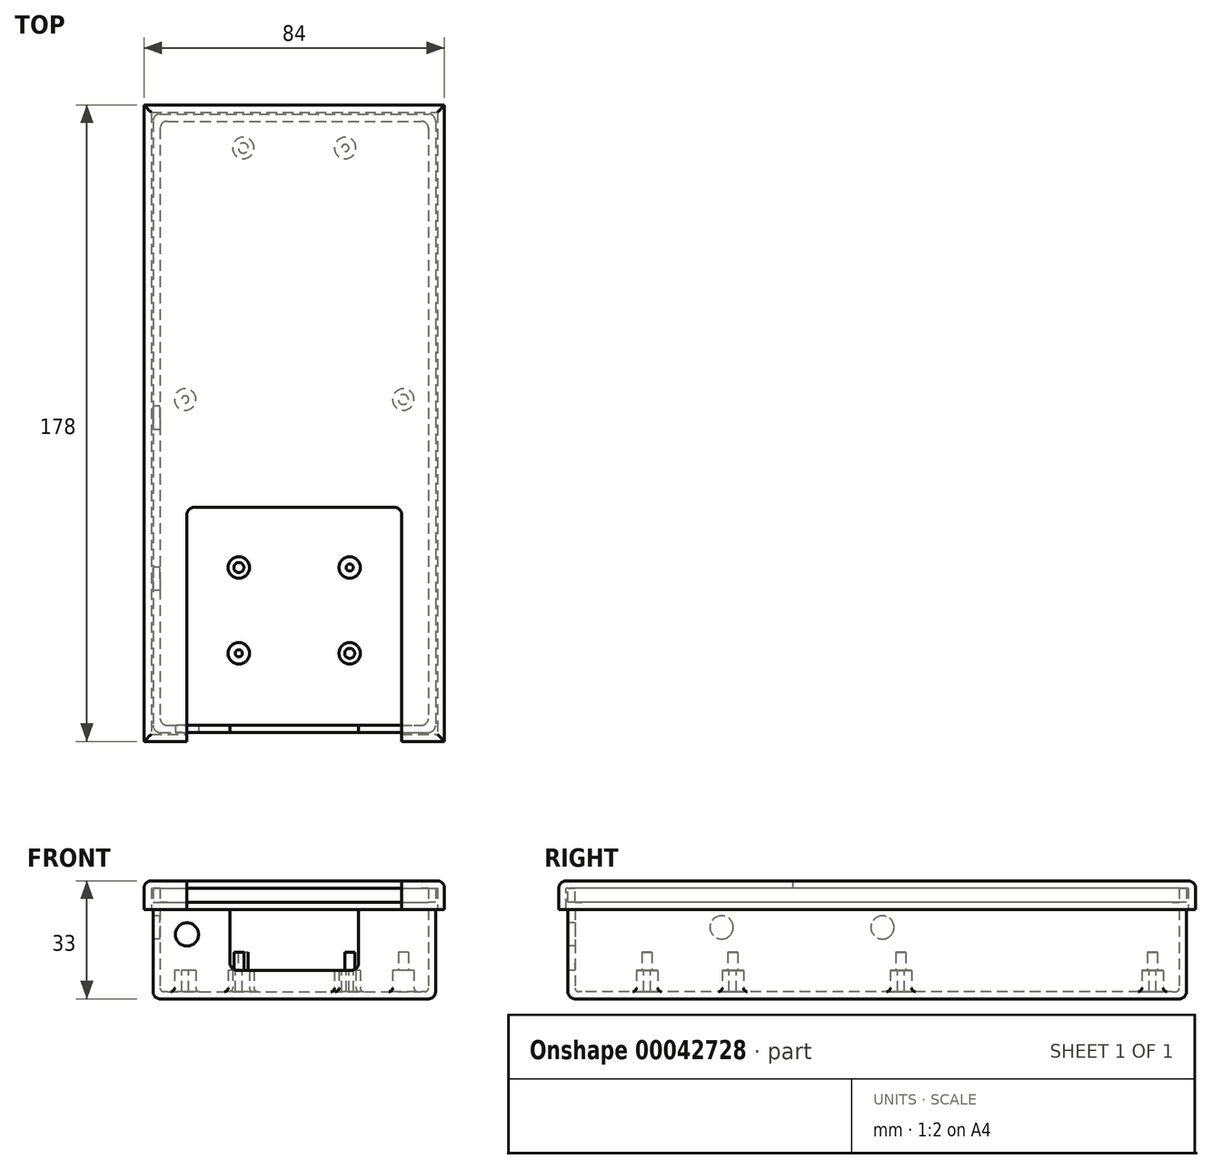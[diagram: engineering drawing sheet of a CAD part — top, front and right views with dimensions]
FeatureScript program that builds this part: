
annotation { "Feature Type Name" : "Feature", "Feature Type Description" : "" }
export const myFeature = defineFeature(function(context is Context, id is Id, definition is map)
    precondition{}
    {
        {
            var Q0;
            Q0=qCreatedBy(makeId("Top.planeOp"),FACE);
            var sketch = newSketch(context, id + "F0", { "sketchPlane" : qUnion([Q0])});
            skLineSegment(sketch, "E0.bottom", {"start": v(-37.5, 83) * mm, "end": v(37.5, 83) * mm});
            skLineSegment(sketch, "E0.top", {"start": v(-37.5, -86) * mm, "end": v(37.5, -86) * mm});
            skLineSegment(sketch, "E0.left", {"start": v(-37.5, 83) * mm, "end": v(-37.5, -86) * mm});
            skLineSegment(sketch, "E0.right", {"start": v(37.5, 83) * mm, "end": v(37.5, -86) * mm});
            skCircle(sketch, "E1", {"center": v(-14.25, 75.5) * mm, "radius": 3 * mm});
            skCircle(sketch, "E2", {"center": v(14.25, 75.5) * mm, "radius": 3 * mm});
            skCircle(sketch, "E3", {"center": v(30.5, 5.15) * mm, "radius": 3 * mm});
            skCircle(sketch, "E4", {"center": v(-30.5, 5.15) * mm, "radius": 3 * mm});
            skLineSegment(sketch, "E5.0", {"start": v(-39.5, 85) * mm, "end": v(39.5, 85) * mm});
            skLineSegment(sketch, "E5.1", {"start": v(-39.5, 85) * mm, "end": v(-39.5, -88) * mm});
            skLineSegment(sketch, "E5.2", {"start": v(-39.5, -88) * mm, "end": v(39.5, -88) * mm});
            skLineSegment(sketch, "E5.3", {"start": v(39.5, 85) * mm, "end": v(39.5, -88) * mm});
            skCircle(sketch, "E6", {"center": v(15.5, -41.85) * mm, "radius": 3 * mm});
            skCircle(sketch, "E7", {"center": v(-15.5, -41.85) * mm, "radius": 3 * mm});
            skCircle(sketch, "E8", {"center": v(15.5, -65.85) * mm, "radius": 3 * mm});
            skCircle(sketch, "E9", {"center": v(-15.5, -65.85) * mm, "radius": 3 * mm});
            skSolve(sketch);
        }
        {
            var Q0;
            Q0=makeQuery(id+"F0.imprint","IMPRINT",FACE,{"disambiguationData":[TD([[makeQuery(id+"F0.imprint","IMPRINT",EDGE,{"derivedFrom":sQuery(id+"F0.wireOp",EDGE,"E0.bottom")}),-1.0]])]});
            extrude(context, id + "F1", {"entities" : qUnion([Q0]), "depth" : 2 * mm});
        }
        {
            var Q0;
            Q0=makeQuery(id+"F0.imprint","IMPRINT",FACE,{"disambiguationData":[TD([[makeQuery(id+"F0.imprint","IMPRINT",EDGE,{"derivedFrom":sQuery(id+"F0.wireOp",EDGE,"E0.bottom")}),1.0]])]});
            extrude(context, id + "F2", {"entities" : qUnion([Q0]), "operationType" : NewBodyOperationType.ADD, "depth" : 25 * mm});
        }
        {
            var Q0;
            Q0=makeQuery(id+"F0.imprint","IMPRINT",FACE,{"disambiguationData":[TD([[makeQuery(id+"F0.imprint","IMPRINT",EDGE,{"derivedFrom":sQuery(id+"F0.wireOp",EDGE,"E1")}),1.0]])]});
            var Q1;
            Q1=makeQuery(id+"F0.imprint","IMPRINT",FACE,{"disambiguationData":[TD([[makeQuery(id+"F0.imprint","IMPRINT",EDGE,{"derivedFrom":sQuery(id+"F0.wireOp",EDGE,"E2")}),1.0]])]});
            var Q2;
            Q2=makeQuery(id+"F0.imprint","IMPRINT",FACE,{"disambiguationData":[TD([[makeQuery(id+"F0.imprint","IMPRINT",EDGE,{"derivedFrom":sQuery(id+"F0.wireOp",EDGE,"E3")}),1.0]])]});
            var Q3;
            Q3=makeQuery(id+"F0.imprint","IMPRINT",FACE,{"disambiguationData":[TD([[makeQuery(id+"F0.imprint","IMPRINT",EDGE,{"derivedFrom":sQuery(id+"F0.wireOp",EDGE,"E4")}),1.0]])]});
            var Q4;
            Q4=makeQuery(id+"F0.imprint","IMPRINT",FACE,{"disambiguationData":[TD([[makeQuery(id+"F0.imprint","IMPRINT",EDGE,{"derivedFrom":sQuery(id+"F0.wireOp",EDGE,"E6")}),1.0]])]});
            var Q5;
            Q5=makeQuery(id+"F0.imprint","IMPRINT",FACE,{"disambiguationData":[TD([[makeQuery(id+"F0.imprint","IMPRINT",EDGE,{"derivedFrom":sQuery(id+"F0.wireOp",EDGE,"E8")}),1.0]])]});
            var Q6;
            Q6=makeQuery(id+"F0.imprint","IMPRINT",FACE,{"disambiguationData":[TD([[makeQuery(id+"F0.imprint","IMPRINT",EDGE,{"derivedFrom":sQuery(id+"F0.wireOp",EDGE,"E7")}),1.0]])]});
            var Q7;
            Q7=makeQuery(id+"F0.imprint","IMPRINT",FACE,{"disambiguationData":[TD([[makeQuery(id+"F0.imprint","IMPRINT",EDGE,{"derivedFrom":sQuery(id+"F0.wireOp",EDGE,"E9")}),1.0]])]});
            extrude(context, id + "F3", {"entities" : qUnion([Q0, Q1, Q2, Q3, Q4, Q5, Q6, Q7]), "operationType" : NewBodyOperationType.ADD, "depth" : 8 * mm});
        }
        {
            var Q0;
            Q0=makeQuery(id+"F3.opExtrude","CAP_FACE",FACE,{"disambiguationData":[OSD([sQuery(id+"F0.wireOp",EDGE,"E1")])],"isStart":false});
            var sketch = newSketch(context, id + "F4", { "sketchPlane" : qUnion([Q0])});
            skCircle(sketch, "E10", {"center": v(-14.25, 75.5) * mm, "radius": 1.4 * mm});
            skCircle(sketch, "E11", {"center": v(30.5, 5.15) * mm, "radius": 1.4 * mm});
            skCircle(sketch, "E12", {"center": v(-15.5, -41.85) * mm, "radius": 1.4 * mm});
            skCircle(sketch, "E13", {"center": v(15.5, -65.85) * mm, "radius": 1.4 * mm});
            skCircle(sketch, "E14", {"center": v(14.25, 75.5) * mm, "radius": 1 * mm});
            skCircle(sketch, "E15", {"center": v(-30.5, 5.15) * mm, "radius": 1 * mm});
            skCircle(sketch, "E16", {"center": v(15.5, -41.85) * mm, "radius": 1 * mm});
            skCircle(sketch, "E17", {"center": v(-15.5, -65.85) * mm, "radius": 1 * mm});
            skSolve(sketch);
        }
        {
            var Q0;
            Q0=makeQuery(id+"F4.imprint","IMPRINT",FACE,{"disambiguationData":[TD([[makeQuery(id+"F4.imprint","IMPRINT",EDGE,{"derivedFrom":sQuery(id+"F4.wireOp",EDGE,"E10")}),1.0]])]});
            var Q1;
            Q1=makeQuery(id+"F4.imprint","IMPRINT",FACE,{"disambiguationData":[TD([[makeQuery(id+"F4.imprint","IMPRINT",EDGE,{"derivedFrom":sQuery(id+"F4.wireOp",EDGE,"E11")}),1.0]])]});
            var Q2;
            Q2=makeQuery(id+"F4.imprint","IMPRINT",FACE,{"disambiguationData":[TD([[makeQuery(id+"F4.imprint","IMPRINT",EDGE,{"derivedFrom":sQuery(id+"F4.wireOp",EDGE,"E12")}),1.0]])]});
            var Q3;
            Q3=makeQuery(id+"F4.imprint","IMPRINT",FACE,{"disambiguationData":[TD([[makeQuery(id+"F4.imprint","IMPRINT",EDGE,{"derivedFrom":sQuery(id+"F4.wireOp",EDGE,"E13")}),1.0]])]});
            var Q4;
            Q4=sQuery(id+"F4.wireOp",EDGE,"E13");
            var Q5;
            Q5=sQuery(id+"F4.wireOp",EDGE,"E12");
            var Q6;
            Q6=sQuery(id+"F4.wireOp",EDGE,"E11");
            var Q7;
            Q7=sQuery(id+"F4.wireOp",EDGE,"E10");
            extrude(context, id + "F5", {"entities" : qUnion([Q0, Q1, Q2, Q3]), "operationType" : NewBodyOperationType.ADD, "surfaceEntities" : qUnion([Q4, Q5, Q6, Q7]), "depth" : 5 * mm});
        }
        {
            var Q0;
            Q0=makeQuery(id+"F4.imprint","IMPRINT",FACE,{"disambiguationData":[TD([[makeQuery(id+"F4.imprint","IMPRINT",EDGE,{"derivedFrom":sQuery(id+"F4.wireOp",EDGE,"E14")}),1.0]])]});
            var Q1;
            Q1=makeQuery(id+"F4.imprint","IMPRINT",FACE,{"disambiguationData":[TD([[makeQuery(id+"F4.imprint","IMPRINT",EDGE,{"derivedFrom":sQuery(id+"F4.wireOp",EDGE,"E15")}),1.0]])]});
            var Q2;
            Q2=makeQuery(id+"F4.imprint","IMPRINT",FACE,{"disambiguationData":[TD([[makeQuery(id+"F4.imprint","IMPRINT",EDGE,{"derivedFrom":sQuery(id+"F4.wireOp",EDGE,"E16")}),1.0]])]});
            var Q3;
            Q3=makeQuery(id+"F4.imprint","IMPRINT",FACE,{"disambiguationData":[TD([[makeQuery(id+"F4.imprint","IMPRINT",EDGE,{"derivedFrom":sQuery(id+"F4.wireOp",EDGE,"E17")}),1.0]])]});
            extrude(context, id + "F6", {"entities" : qUnion([Q0, Q1, Q2, Q3]), "operationType" : NewBodyOperationType.REMOVE, "oppositeDirection" : true, "depth" : 6 * mm});
        }
        {
            var Q0;
            Q0=makeQuery(id+"F2.opExtrude","SWEPT_FACE",FACE,{"disambiguationData":[OSD([sQuery(id+"F0.wireOp",EDGE,"E5.2")])]});
            var sketch = newSketch(context, id + "F7", { "sketchPlane" : qUnion([Q0])});
            skLineSegment(sketch, "E18.bottom", {"start": v(-18, 25) * mm, "end": v(18, 25) * mm});
            skLineSegment(sketch, "E18.top", {"start": v(-18, 8) * mm, "end": v(18, 8) * mm});
            skLineSegment(sketch, "E18.left", {"start": v(-18, 25) * mm, "end": v(-18, 8) * mm});
            skLineSegment(sketch, "E18.right", {"start": v(18, 25) * mm, "end": v(18, 8) * mm});
            skSolve(sketch);
        }
        {
            var Q0;
            Q0=makeQuery(id+"F7.imprint","IMPRINT",FACE,{"disambiguationData":[TD([[makeQuery(id+"F7.imprint","IMPRINT",EDGE,{"derivedFrom":sQuery(id+"F7.wireOp",EDGE,"E18.bottom")}),-1.0]])]});
            extrude(context, id + "F8", {"entities" : qUnion([Q0]), "operationType" : NewBodyOperationType.REMOVE, "endBound" : BoundingType.UP_TO_NEXT, "oppositeDirection" : true, "depth" : 25 * mm});
        }
        {
            var Q0;
            {var subQ0=sQuery(id+"F0.wireOp",EDGE,"E0.bottom");var subQ1=sQuery(id+"F0.wireOp",EDGE,"E0.top");var subQ2=sQuery(id+"F0.wireOp",EDGE,"E0.left");var subQ3=sQuery(id+"F0.wireOp",EDGE,"E0.right");var subQ4=sQuery(id+"F0.wireOp",EDGE,"E1");var subQ5=sQuery(id+"F0.wireOp",EDGE,"E2");var subQ6=sQuery(id+"F0.wireOp",EDGE,"E3");var subQ7=sQuery(id+"F0.wireOp",EDGE,"E4");var subQ8=sQuery(id+"F0.wireOp",EDGE,"E6");var subQ9=sQuery(id+"F0.wireOp",EDGE,"E7");var subQ10=sQuery(id+"F0.wireOp",EDGE,"E8");var subQ11=sQuery(id+"F0.wireOp",EDGE,"E9");Q0=makeQuery(id+"F3.boolean.opBoolean","MERGE",FACE,{"derivedFrom":[makeQuery(id+"F2.boolean.opBoolean","MERGE",FACE,{"derivedFrom":[makeQuery(id+"F1.opExtrude","CAP_FACE",FACE,{"disambiguationData":[OSD([subQ0,subQ1,subQ2,subQ3,subQ4,subQ5,subQ6,subQ7,subQ8,subQ9,subQ10,subQ11])],"isStart":true}),makeQuery(id+"F2.opExtrude","CAP_FACE",FACE,{"disambiguationData":[OSD([subQ0,subQ1,subQ2,subQ3,sQuery(id+"F0.wireOp",EDGE,"E5.0"),sQuery(id+"F0.wireOp",EDGE,"E5.1"),sQuery(id+"F0.wireOp",EDGE,"E5.2"),sQuery(id+"F0.wireOp",EDGE,"E5.3")])],"isStart":true})]}),makeQuery(id+"F3.opExtrude","CAP_FACE",FACE,{"disambiguationData":[OSD([subQ4])],"isStart":true}),makeQuery(id+"F3.opExtrude","CAP_FACE",FACE,{"disambiguationData":[OSD([subQ5])],"isStart":true}),makeQuery(id+"F3.opExtrude","CAP_FACE",FACE,{"disambiguationData":[OSD([subQ6])],"isStart":true}),makeQuery(id+"F3.opExtrude","CAP_FACE",FACE,{"disambiguationData":[OSD([subQ7])],"isStart":true}),makeQuery(id+"F3.opExtrude","CAP_FACE",FACE,{"disambiguationData":[OSD([subQ8])],"isStart":true}),makeQuery(id+"F3.opExtrude","CAP_FACE",FACE,{"disambiguationData":[OSD([subQ9])],"isStart":true}),makeQuery(id+"F3.opExtrude","CAP_FACE",FACE,{"disambiguationData":[OSD([subQ10])],"isStart":true}),makeQuery(id+"F3.opExtrude","CAP_FACE",FACE,{"disambiguationData":[OSD([subQ11])],"isStart":true})]});}
            var sketch = newSketch(context, id + "F9", { "sketchPlane" : qUnion([Q0])});
            skCircle(sketch, "E19", {"center": v(-30, 75) * mm, "radius": 3 * mm});
            skCircle(sketch, "E20", {"center": v(30, 75) * mm, "radius": 3 * mm});
            skCircle(sketch, "E21", {"center": v(-30, -75) * mm, "radius": 3 * mm});
            skCircle(sketch, "E22", {"center": v(30, -75) * mm, "radius": 3 * mm});
            skLineSegment(sketch, "E23", {"start": v(-55.2, 75) * mm, "end": v(65.62, 75) * mm, "construction": true});
            skLineSegment(sketch, "E24", {"start": v(-55.2, -75) * mm, "end": v(62.26, -75) * mm, "construction": true});
            skSolve(sketch);
        }
        {
            var Q0;
            Q0=makeQuery(id+"F2.opExtrude","CAP_EDGE",EDGE,{"disambiguationData":[OSD([sQuery(id+"F0.wireOp",EDGE,"E5.1")])],"isStart":true});
            var Q1;
            Q1=makeQuery(id+"F2.opExtrude","CAP_EDGE",EDGE,{"disambiguationData":[OSD([sQuery(id+"F0.wireOp",EDGE,"E5.3")])],"isStart":true});
            var Q2;
            Q2=makeQuery(id+"F2.opExtrude","CAP_EDGE",EDGE,{"disambiguationData":[OSD([sQuery(id+"F0.wireOp",EDGE,"E5.2")])],"isStart":true});
            var Q3;
            Q3=makeQuery(id+"F2.opExtrude","CAP_EDGE",EDGE,{"disambiguationData":[OSD([sQuery(id+"F0.wireOp",EDGE,"E5.0")])],"isStart":true});
            var Q4;
            Q4=makeQuery(id+"F2.opExtrude","SWEPT_EDGE",EDGE,{"disambiguationData":[OSD([sQuery(id+"F0.wireOp",EDGE,"E0.bottom"),sQuery(id+"F0.wireOp",EDGE,"E0.right")])]});
            var Q5;
            Q5=makeQuery(id+"F2.opExtrude","SWEPT_EDGE",EDGE,{"disambiguationData":[OSD([sQuery(id+"F0.wireOp",EDGE,"E0.bottom"),sQuery(id+"F0.wireOp",EDGE,"E0.left")])]});
            var Q6;
            Q6=makeQuery(id+"F2.opExtrude","SWEPT_EDGE",EDGE,{"disambiguationData":[OSD([sQuery(id+"F0.wireOp",EDGE,"E0.top"),sQuery(id+"F0.wireOp",EDGE,"E0.left")])]});
            var Q7;
            Q7=makeQuery(id+"F2.opExtrude","SWEPT_EDGE",EDGE,{"disambiguationData":[OSD([sQuery(id+"F0.wireOp",EDGE,"E0.top"),sQuery(id+"F0.wireOp",EDGE,"E0.right")])]});
            var Q8;
            Q8=makeQuery(id+"F2.opExtrude","SWEPT_EDGE",EDGE,{"disambiguationData":[OSD([sQuery(id+"F0.wireOp",EDGE,"E5.2"),sQuery(id+"F0.wireOp",EDGE,"E5.3")])]});
            var Q9;
            Q9=makeQuery(id+"F2.opExtrude","SWEPT_EDGE",EDGE,{"disambiguationData":[OSD([sQuery(id+"F0.wireOp",EDGE,"E5.0"),sQuery(id+"F0.wireOp",EDGE,"E5.3")])]});
            var Q10;
            Q10=makeQuery(id+"F2.opExtrude","SWEPT_EDGE",EDGE,{"disambiguationData":[OSD([sQuery(id+"F0.wireOp",EDGE,"E5.0"),sQuery(id+"F0.wireOp",EDGE,"E5.1")])]});
            var Q11;
            Q11=makeQuery(id+"F2.opExtrude","SWEPT_EDGE",EDGE,{"disambiguationData":[OSD([sQuery(id+"F0.wireOp",EDGE,"E5.1"),sQuery(id+"F0.wireOp",EDGE,"E5.2")])]});
            fillet(context, id + "F10", {"entities" : qUnion([Q0, Q1, Q2, Q3, Q4, Q5, Q6, Q7, Q8, Q9, Q10, Q11]), "radius" : 2 * mm, "tangentPropagation" : true, "allowEdgeOverflow" : false});
        }
        {
            var Q0;
            Q0=makeQuery(id+"F1.opExtrude","CAP_EDGE",EDGE,{"disambiguationData":[OSD([sQuery(id+"F0.wireOp",EDGE,"E7")])],"isStart":false});
            var Q1;
            Q1=makeQuery(id+"F1.opExtrude","CAP_EDGE",EDGE,{"disambiguationData":[OSD([sQuery(id+"F0.wireOp",EDGE,"E4")])],"isStart":false});
            var Q2;
            Q2=makeQuery(id+"F1.opExtrude","CAP_EDGE",EDGE,{"disambiguationData":[OSD([sQuery(id+"F0.wireOp",EDGE,"E1")])],"isStart":false});
            var Q3;
            Q3=makeQuery(id+"F1.opExtrude","CAP_EDGE",EDGE,{"disambiguationData":[OSD([sQuery(id+"F0.wireOp",EDGE,"E2")])],"isStart":false});
            var Q4;
            Q4=makeQuery(id+"F1.opExtrude","CAP_FACE",FACE,{"disambiguationData":[OSD([sQuery(id+"F0.wireOp",EDGE,"E0.bottom"),sQuery(id+"F0.wireOp",EDGE,"E0.top"),sQuery(id+"F0.wireOp",EDGE,"E0.left"),sQuery(id+"F0.wireOp",EDGE,"E0.right"),sQuery(id+"F0.wireOp",EDGE,"E1"),sQuery(id+"F0.wireOp",EDGE,"E2"),sQuery(id+"F0.wireOp",EDGE,"E3"),sQuery(id+"F0.wireOp",EDGE,"E4"),sQuery(id+"F0.wireOp",EDGE,"E6"),sQuery(id+"F0.wireOp",EDGE,"E7"),sQuery(id+"F0.wireOp",EDGE,"E8"),sQuery(id+"F0.wireOp",EDGE,"E9")])],"isStart":false});
            fillet(context, id + "F11", {"entities" : qUnion([Q0, Q1, Q2, Q3, Q4]), "radius" : 1 * mm, "tangentPropagation" : true, "allowEdgeOverflow" : false});
        }
        {
            var Q0;
            Q0=makeQuery(id+"F8.boolean.opBoolean","COPY",EDGE,{"derivedFrom":makeQuery(id+"F8.opExtrude","SWEPT_EDGE",EDGE,{"disambiguationData":[OSD([sQuery(id+"F7.wireOp",EDGE,"E18.top"),sQuery(id+"F7.wireOp",EDGE,"E18.left")])]})});
            var Q1;
            Q1=makeQuery(id+"F8.boolean.opBoolean","COPY",EDGE,{"derivedFrom":makeQuery(id+"F8.opExtrude","SWEPT_EDGE",EDGE,{"disambiguationData":[OSD([sQuery(id+"F7.wireOp",EDGE,"E18.top"),sQuery(id+"F7.wireOp",EDGE,"E18.right")])]})});
            var Q2;
            Q2=makeQuery(id+"F8.boolean.opBoolean","COPY",EDGE,{"derivedFrom":makeQuery(id+"F8.opExtrude","SWEPT_EDGE",EDGE,{"disambiguationData":[OSD([sQuery(id+"F0.wireOp",EDGE,"E5.2"),sQuery(id+"F7.wireOp",EDGE,"E18.bottom"),sQuery(id+"F7.wireOp",EDGE,"E18.right")])]})});
            var Q3;
            Q3=makeQuery(id+"F8.boolean.opBoolean","COPY",EDGE,{"derivedFrom":makeQuery(id+"F8.opExtrude","SWEPT_EDGE",EDGE,{"disambiguationData":[OSD([sQuery(id+"F0.wireOp",EDGE,"E5.2"),sQuery(id+"F7.wireOp",EDGE,"E18.bottom"),sQuery(id+"F7.wireOp",EDGE,"E18.left")])]})});
            fillet(context, id + "F12", {"entities" : qUnion([Q0, Q1, Q2, Q3]), "radius" : 2 * mm, "tangentPropagation" : true, "allowEdgeOverflow" : false});
        }
        {
            var Q0;
            Q0=makeQuery(id+"F2.opExtrude","SWEPT_FACE",FACE,{"disambiguationData":[OSD([sQuery(id+"F0.wireOp",EDGE,"E5.1")])]});
            var sketch = newSketch(context, id + "F13", { "sketchPlane" : qUnion([Q0])});
            skCircle(sketch, "E25", {"center": v(0, 20) * mm, "radius": 3.25 * mm});
            skCircle(sketch, "E26", {"center": v(45, 20) * mm, "radius": 3.25 * mm});
            skSolve(sketch);
        }
        {
            var Q0;
            Q0=makeQuery(id+"F13.imprint","IMPRINT",FACE,{"disambiguationData":[TD([[makeQuery(id+"F13.imprint","IMPRINT",EDGE,{"derivedFrom":sQuery(id+"F13.wireOp",EDGE,"E25")}),1.0]])]});
            var Q1;
            Q1=makeQuery(id+"F13.imprint","IMPRINT",FACE,{"disambiguationData":[TD([[makeQuery(id+"F13.imprint","IMPRINT",EDGE,{"derivedFrom":sQuery(id+"F13.wireOp",EDGE,"E26")}),1.0]])]});
            extrude(context, id + "F14", {"entities" : qUnion([Q0, Q1]), "operationType" : NewBodyOperationType.REMOVE, "endBound" : BoundingType.UP_TO_NEXT, "oppositeDirection" : true, "depth" : 25 * mm});
        }
        {
            var Q0;
            Q0=makeQuery(id+"F2.opExtrude","SWEPT_FACE",FACE,{"disambiguationData":[OSD([sQuery(id+"F0.wireOp",EDGE,"E5.2")])]});
            var sketch = newSketch(context, id + "F15", { "sketchPlane" : qUnion([Q0])});
            skCircle(sketch, "E27", {"center": v(-30, 18) * mm, "radius": 3.25 * mm});
            skSolve(sketch);
        }
        {
            var Q0;
            Q0=makeQuery(id+"F15.imprint","IMPRINT",FACE,{"disambiguationData":[TD([[makeQuery(id+"F15.imprint","IMPRINT",EDGE,{"derivedFrom":sQuery(id+"F15.wireOp",EDGE,"E27")}),1.0]])]});
            extrude(context, id + "F16", {"entities" : qUnion([Q0]), "operationType" : NewBodyOperationType.REMOVE, "endBound" : BoundingType.UP_TO_NEXT, "oppositeDirection" : true, "depth" : 25 * mm});
        }
        {
            var Q0;
            Q0=makeQuery(id+"F2.opExtrude","CAP_FACE",FACE,{"disambiguationData":[OSD([sQuery(id+"F0.wireOp",EDGE,"E0.bottom"),sQuery(id+"F0.wireOp",EDGE,"E0.top"),sQuery(id+"F0.wireOp",EDGE,"E0.left"),sQuery(id+"F0.wireOp",EDGE,"E0.right"),sQuery(id+"F0.wireOp",EDGE,"E5.0"),sQuery(id+"F0.wireOp",EDGE,"E5.1"),sQuery(id+"F0.wireOp",EDGE,"E5.2"),sQuery(id+"F0.wireOp",EDGE,"E5.3")])],"isStart":false});
            var sketch = newSketch(context, id + "F17", { "sketchPlane" : qUnion([Q0])});
            skLineSegment(sketch, "E28.bottom", {"start": v(-40, 85.5) * mm, "end": v(40, 85.5) * mm});
            skLineSegment(sketch, "E28.top", {"start": v(-40, -88.5) * mm, "end": v(40, -88.5) * mm});
            skLineSegment(sketch, "E28.left", {"start": v(-40, 85.5) * mm, "end": v(-40, -88.5) * mm});
            skLineSegment(sketch, "E28.right", {"start": v(40, 85.5) * mm, "end": v(40, -88.5) * mm});
            skLineSegment(sketch, "E29.0", {"start": v(-42, 87.5) * mm, "end": v(42, 87.5) * mm});
            skLineSegment(sketch, "E29.1", {"start": v(-42, 87.5) * mm, "end": v(-42, -90.5) * mm});
            skLineSegment(sketch, "E29.2", {"start": v(-42, -90.5) * mm, "end": v(42, -90.5) * mm});
            skLineSegment(sketch, "E29.3", {"start": v(42, 87.5) * mm, "end": v(42, -90.5) * mm});
            skSolve(sketch);
        }
        {
            var Q0;
            Q0 = qSketchRegion(id + "F17", true);
            var Q1;
            Q1=makeQuery(id+"F17.imprint","IMPRINT",FACE,{"disambiguationData":[TD([[makeQuery(id+"F17.imprint","IMPRINT",EDGE,{"derivedFrom":sQuery(id+"F17.wireOp",EDGE,"E28.bottom")}),-1.0]])]});
            var Q2;
            {var subQ6=sQuery(id+"F0.wireOp",EDGE,"E0.bottom");Q2=makeQuery(id+"F17.imprint","IMPRINT",FACE,{"disambiguationData":[TD([[makeQuery(id+"F17.imprint","IMPRINT",EDGE,{"derivedFrom":makeQuery(id+"F2.opExtrude","CAP_EDGE",EDGE,{"disambiguationData":[OSD([subQ6])],"isStart":false})}),1.0]])]});}
            extrude(context, id + "F18", {"entities" : qUnion([Q0, Q1, Q2]), "depth" : 8 * mm});
        }
        {
            var Q0;
            Q0=makeQuery(id+"F17.imprint","IMPRINT",FACE,{"disambiguationData":[TD([[makeQuery(id+"F17.imprint","IMPRINT",EDGE,{"derivedFrom":sQuery(id+"F17.wireOp",EDGE,"E28.bottom")}),-1.0]])]});
            extrude(context, id + "F19", {"entities" : qUnion([Q0]), "operationType" : NewBodyOperationType.REMOVE, "depth" : 6 * mm});
        }
        {
            var Q0;
            {var subQ6=sQuery(id+"F0.wireOp",EDGE,"E0.bottom");Q0=makeQuery(id+"F17.imprint","IMPRINT",FACE,{"disambiguationData":[TD([[makeQuery(id+"F17.imprint","IMPRINT",EDGE,{"derivedFrom":makeQuery(id+"F2.opExtrude","CAP_EDGE",EDGE,{"disambiguationData":[OSD([subQ6])],"isStart":false})}),1.0]])]});}
            extrude(context, id + "F20", {"entities" : qUnion([Q0]), "operationType" : NewBodyOperationType.REMOVE, "depth" : 2 * mm});
        }
        {
            var Q0;
            Q0=makeQuery(id+"F18.opExtrude","CAP_FACE",FACE,{"disambiguationData":[OSD([sQuery(id+"F17.wireOp",EDGE,"E29.0"),sQuery(id+"F17.wireOp",EDGE,"E29.1"),sQuery(id+"F17.wireOp",EDGE,"E29.2"),sQuery(id+"F17.wireOp",EDGE,"E29.3")])],"isStart":false});
            var sketch = newSketch(context, id + "F21", { "sketchPlane" : qUnion([Q0])});
            skLineSegment(sketch, "E30.bottom", {"start": v(-30, -90.5) * mm, "end": v(30, -90.5) * mm});
            skLineSegment(sketch, "E30.top", {"start": v(-30, -25) * mm, "end": v(30, -25) * mm});
            skLineSegment(sketch, "E30.left", {"start": v(-30, -90.5) * mm, "end": v(-30, -25) * mm});
            skLineSegment(sketch, "E30.right", {"start": v(30, -90.5) * mm, "end": v(30, -25) * mm});
            skSolve(sketch);
        }
        {
            var Q0;
            Q0=makeQuery(id+"F21.imprint","IMPRINT",FACE,{"disambiguationData":[TD([[makeQuery(id+"F21.imprint","IMPRINT",EDGE,{"derivedFrom":sQuery(id+"F21.wireOp",EDGE,"E30.bottom")}),1.0]])]});
            extrude(context, id + "F22", {"entities" : qUnion([Q0]), "operationType" : NewBodyOperationType.REMOVE, "endBound" : BoundingType.UP_TO_NEXT, "oppositeDirection" : true, "depth" : 25 * mm});
        }
        {
            var Q0;
            Q0=makeQuery(id+"F18.opExtrude","CAP_EDGE",EDGE,{"disambiguationData":[OSD([sQuery(id+"F17.wireOp",EDGE,"E29.1")])],"isStart":false});
            var Q1;
            Q1=makeQuery(id+"F18.opExtrude","CAP_EDGE",EDGE,{"disambiguationData":[OSD([sQuery(id+"F17.wireOp",EDGE,"E29.3")])],"isStart":false});
            var Q2;
            {var subQ0=sQuery(id+"F17.wireOp",EDGE,"E29.2");var subQ1=sQuery(id+"F17.wireOp",EDGE,"E29.3");Q2=makeQuery(id+"F22.boolean.opBoolean","SPLIT",EDGE,{"disambiguationData":[TD([makeQuery(id+"F18.opExtrude","SWEPT_FACE",FACE,{"disambiguationData":[OSD([subQ1])]})])],"derivedFrom":makeQuery(id+"F18.opExtrude","CAP_EDGE",EDGE,{"disambiguationData":[OSD([subQ0])],"isStart":false})});}
            var Q3;
            {var subQ0=sQuery(id+"F17.wireOp",EDGE,"E29.2");var subQ1=sQuery(id+"F17.wireOp",EDGE,"E29.1");Q3=makeQuery(id+"F22.boolean.opBoolean","SPLIT",EDGE,{"disambiguationData":[TD([makeQuery(id+"F18.opExtrude","SWEPT_FACE",FACE,{"disambiguationData":[OSD([subQ1])]})])],"derivedFrom":makeQuery(id+"F18.opExtrude","CAP_EDGE",EDGE,{"disambiguationData":[OSD([subQ0])],"isStart":false})});}
            var Q4;
            Q4=makeQuery(id+"F18.opExtrude","CAP_EDGE",EDGE,{"disambiguationData":[OSD([sQuery(id+"F17.wireOp",EDGE,"E29.0")])],"isStart":false});
            var Q5;
            Q5=makeQuery(id+"F22.boolean.opBoolean","COPY",EDGE,{"derivedFrom":makeQuery(id+"F22.opExtrude","SWEPT_EDGE",EDGE,{"disambiguationData":[OSD([sQuery(id+"F21.wireOp",EDGE,"E30.top"),sQuery(id+"F21.wireOp",EDGE,"E30.left")])]})});
            var Q6;
            Q6=makeQuery(id+"F22.boolean.opBoolean","COPY",EDGE,{"derivedFrom":makeQuery(id+"F22.opExtrude","SWEPT_EDGE",EDGE,{"disambiguationData":[OSD([sQuery(id+"F21.wireOp",EDGE,"E30.top"),sQuery(id+"F21.wireOp",EDGE,"E30.right")])]})});
            var Q7;
            Q7=makeQuery(id+"F22.boolean.opBoolean","COPY",EDGE,{"derivedFrom":makeQuery(id+"F22.opExtrude","CAP_EDGE",EDGE,{"disambiguationData":[OSD([sQuery(id+"F21.wireOp",EDGE,"E30.left")])],"isStart":true})});
            fillet(context, id + "F23", {"entities" : qUnion([Q0, Q1, Q2, Q3, Q4, Q5, Q6, Q7]), "radius" : 2 * mm, "tangentPropagation" : true, "allowEdgeOverflow" : false});
        }
    });
